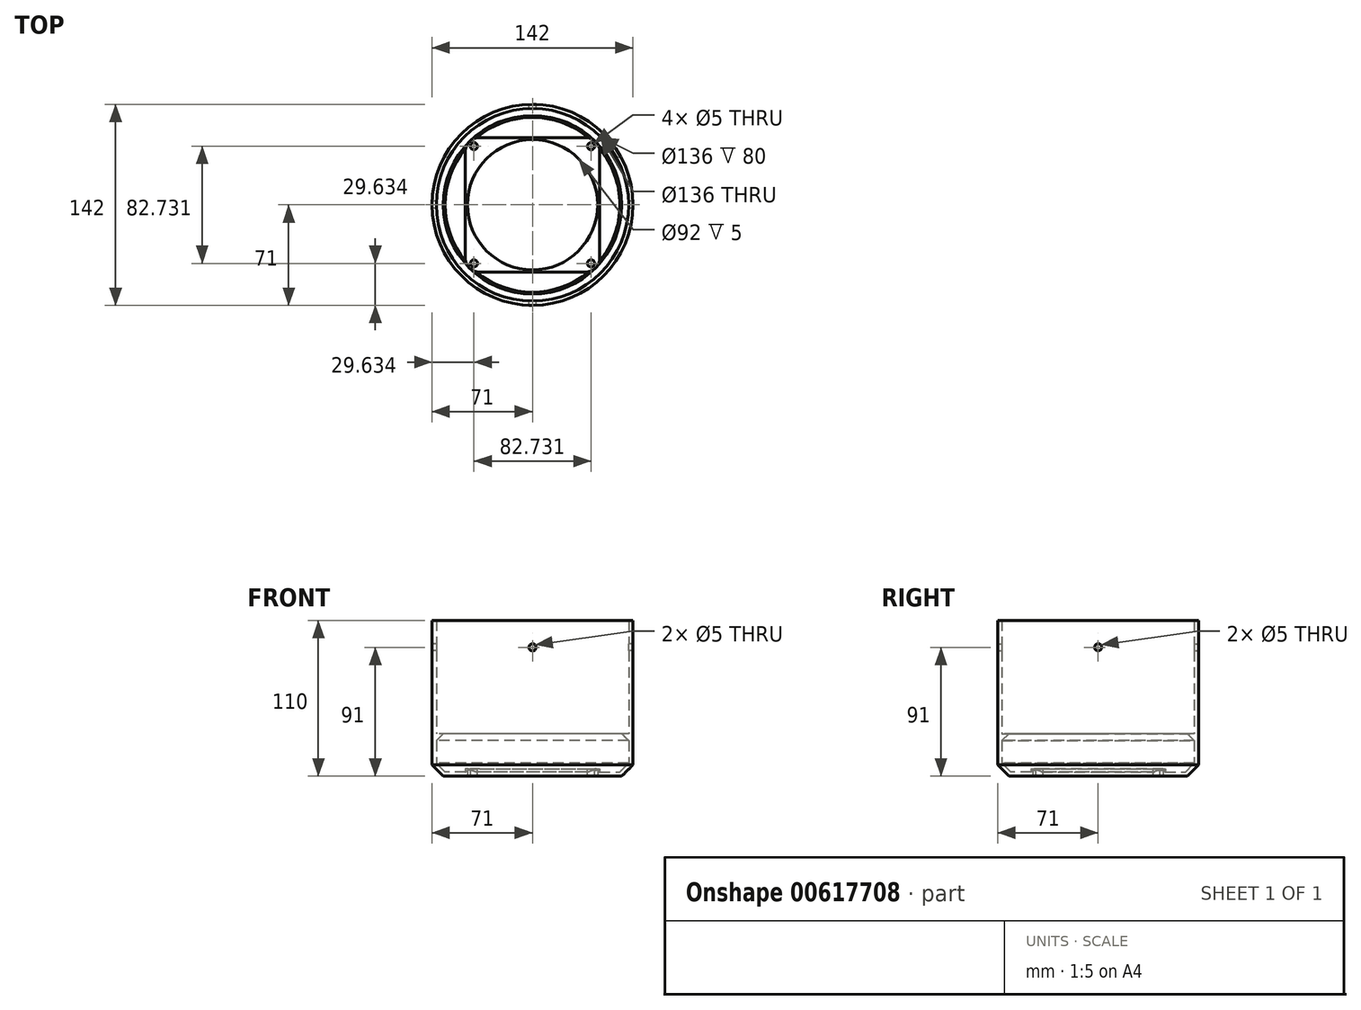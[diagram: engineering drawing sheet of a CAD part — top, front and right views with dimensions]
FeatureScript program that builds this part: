
annotation { "Feature Type Name" : "Feature", "Feature Type Description" : "" }
export const myFeature = defineFeature(function(context is Context, id is Id, definition is map)
    precondition{}
    {
        {
            var Q0;
            Q0=qCreatedBy(makeId("Top.planeOp"),FACE);
            var sketch = newSketch(context, id + "F0", { "sketchPlane" : qUnion([Q0])});
            skCircle(sketch, "E0", {"center": v(0, 0) * mm, "radius": 71 * mm});
            skSolve(sketch);
        }
        {
            var Q0;
            Q0=makeQuery(id+"F0.imprint","IMPRINT",FACE,{"disambiguationData":[TD([[makeQuery(id+"F0.imprint","IMPRINT",EDGE,{"derivedFrom":sQuery(id+"F0.wireOp",EDGE,"E0")}),1.0]])]});
            var Q1;
            Q1=sQuery(id+"F0.wireOp",EDGE,"E0");
            extrude(context, id + "F1", {"entities" : qUnion([Q0]), "surfaceEntities" : qUnion([Q1]), "depth" : 50 * mm, "offsetDistance" : 25 * mm});
        }
        {
            var Q0;
            Q0=makeQuery(id+"F1.opExtrude","CAP_EDGE",EDGE,{"disambiguationData":[OSD([sQuery(id+"F0.wireOp",EDGE,"E0")])],"isStart":true});
            chamfer(context, id + "F2", {"entities" : qUnion([Q0]), "width" : 8 * mm, "tangentPropagation" : true});
        }
        {
            var Q0;
            Q0=makeQuery(id+"F1.opExtrude","CAP_FACE",FACE,{"disambiguationData":[OSD([sQuery(id+"F0.wireOp",EDGE,"E0")])],"isStart":false});
            shell(context, id + "F3", {"entities" : qUnion([Q0]), "thickness" : 3 * mm});
        }
        {
            var Q0;
            Q0=makeQuery(id+"F1.opExtrude","CAP_FACE",FACE,{"disambiguationData":[OSD([sQuery(id+"F0.wireOp",EDGE,"E0")])],"isStart":true});
            var sketch = newSketch(context, id + "F4", { "sketchPlane" : qUnion([Q0])});
            skLineSegment(sketch, "E1.bottom", {"start": v(-37.5, 47.5) * mm, "end": v(37.5, 47.5) * mm});
            skLineSegment(sketch, "E1.top", {"start": v(-37.5, -47.5) * mm, "end": v(37.5, -47.5) * mm});
            skLineSegment(sketch, "E1.left", {"start": v(-47.5, 37.5) * mm, "end": v(-47.5, -37.5) * mm});
            skLineSegment(sketch, "E1.right", {"start": v(47.5, 37.5) * mm, "end": v(47.5, -37.5) * mm});
            skPoint(sketch, "E1.middle", {"position": v(0, 0) * mm});
            skLineSegment(sketch, "E2.bottom", {"start": v(-41.37, 41.37) * mm, "end": v(41.37, 41.37) * mm, "construction": true});
            skLineSegment(sketch, "E2.top", {"start": v(-41.37, -41.37) * mm, "end": v(41.37, -41.37) * mm, "construction": true});
            skLineSegment(sketch, "E2.left", {"start": v(-41.37, 41.37) * mm, "end": v(-41.37, -41.37) * mm, "construction": true});
            skLineSegment(sketch, "E2.right", {"start": v(41.37, 41.37) * mm, "end": v(41.37, -41.37) * mm, "construction": true});
            skCircle(sketch, "E3", {"center": v(0, 0) * mm, "radius": 46 * mm});
            skCircle(sketch, "E4", {"center": v(-41.37, 41.37) * mm, "radius": 2.5 * mm});
            skCircle(sketch, "E5", {"center": v(41.37, 41.37) * mm, "radius": 2.5 * mm});
            skCircle(sketch, "E6", {"center": v(41.37, -41.37) * mm, "radius": 2.5 * mm});
            skCircle(sketch, "E7", {"center": v(-41.37, -41.37) * mm, "radius": 2.5 * mm});
            skPoint(sketch, "E8.visualSharp", {"position": v(-47.5, 47.5) * mm});
            skArc(sketch, "E8.filletArc", {"start": v(-37.5, 47.5) * mm, "mid": v(-44.57, 44.57) * mm, "end": v(-47.5, 37.5) * mm});
            skPoint(sketch, "E9.visualSharp", {"position": v(47.5, 47.5) * mm});
            skArc(sketch, "E9.filletArc", {"start": v(47.5, 37.5) * mm, "mid": v(44.57, 44.57) * mm, "end": v(37.5, 47.5) * mm});
            skPoint(sketch, "E10.visualSharp", {"position": v(47.5, -47.5) * mm});
            skArc(sketch, "E10.filletArc", {"start": v(37.5, -47.5) * mm, "mid": v(44.57, -44.57) * mm, "end": v(47.5, -37.5) * mm});
            skPoint(sketch, "E11.visualSharp", {"position": v(-47.5, -47.5) * mm});
            skArc(sketch, "E11.filletArc", {"start": v(-47.5, -37.5) * mm, "mid": v(-44.57, -44.57) * mm, "end": v(-37.5, -47.5) * mm});
            skSolve(sketch);
        }
        {
            var Q0;
            Q0=makeQuery(id+"F4.imprint","IMPRINT",FACE,{"disambiguationData":[TD([[makeQuery(id+"F4.imprint","IMPRINT",EDGE,{"derivedFrom":sQuery(id+"F4.wireOp",EDGE,"E1.bottom")}),-1.0]])]});
            var Q1;
            Q1=makeQuery(id+"F4.imprint","IMPRINT",FACE,{"disambiguationData":[TD([[makeQuery(id+"F4.imprint","IMPRINT",EDGE,{"derivedFrom":sQuery(id+"F4.wireOp",EDGE,"E4")}),1.0]])]});
            var Q2;
            Q2=makeQuery(id+"F4.imprint","IMPRINT",FACE,{"disambiguationData":[TD([[makeQuery(id+"F4.imprint","IMPRINT",EDGE,{"derivedFrom":sQuery(id+"F4.wireOp",EDGE,"E5")}),1.0]])]});
            var Q3;
            Q3=makeQuery(id+"F4.imprint","IMPRINT",FACE,{"disambiguationData":[TD([[makeQuery(id+"F4.imprint","IMPRINT",EDGE,{"derivedFrom":sQuery(id+"F4.wireOp",EDGE,"E6")}),1.0]])]});
            var Q4;
            Q4=makeQuery(id+"F4.imprint","IMPRINT",FACE,{"disambiguationData":[TD([[makeQuery(id+"F4.imprint","IMPRINT",EDGE,{"derivedFrom":sQuery(id+"F4.wireOp",EDGE,"E7")}),1.0]])]});
            extrude(context, id + "F5", {"entities" : qUnion([Q0, Q1, Q2, Q3, Q4]), "operationType" : NewBodyOperationType.ADD, "oppositeDirection" : true, "depth" : 5 * mm, "offsetDistance" : 25 * mm});
        }
        {
            var Q0;
            Q0=makeQuery(id+"F4.imprint","IMPRINT",FACE,{"disambiguationData":[TD([[makeQuery(id+"F4.imprint","IMPRINT",EDGE,{"derivedFrom":sQuery(id+"F4.wireOp",EDGE,"E4")}),1.0]])]});
            var Q1;
            Q1=makeQuery(id+"F4.imprint","IMPRINT",FACE,{"disambiguationData":[TD([[makeQuery(id+"F4.imprint","IMPRINT",EDGE,{"derivedFrom":sQuery(id+"F4.wireOp",EDGE,"E5")}),1.0]])]});
            var Q2;
            Q2=makeQuery(id+"F4.imprint","IMPRINT",FACE,{"disambiguationData":[TD([[makeQuery(id+"F4.imprint","IMPRINT",EDGE,{"derivedFrom":sQuery(id+"F4.wireOp",EDGE,"E6")}),1.0]])]});
            var Q3;
            Q3=makeQuery(id+"F4.imprint","IMPRINT",FACE,{"disambiguationData":[TD([[makeQuery(id+"F4.imprint","IMPRINT",EDGE,{"derivedFrom":sQuery(id+"F4.wireOp",EDGE,"E7")}),1.0]])]});
            var Q4;
            Q4=makeQuery(id+"F4.imprint","IMPRINT",FACE,{"disambiguationData":[TD([[makeQuery(id+"F4.imprint","IMPRINT",EDGE,{"derivedFrom":sQuery(id+"F4.wireOp",EDGE,"E3")}),1.0]])]});
            extrude(context, id + "F6", {"entities" : qUnion([Q0, Q1, Q2, Q3, Q4]), "operationType" : NewBodyOperationType.REMOVE, "endBound" : BoundingType.SYMMETRIC, "depth" : 25 * mm, "offsetDistance" : 25 * mm});
        }
        {
            var Q0;
            Q0=qCreatedBy(makeId("Top.planeOp"),FACE);
            cPlane(context, id + "F7", {"entities" : qUnion([Q0]), "cplaneType" : CPlaneType.OFFSET, "offset" : 25 * mm, "width" : 150 * mm, "height" : 150 * mm});
        }
        {
            var Q0;
            Q0=qCreatedBy(id+"F7.planeOp",FACE);
            var sketch = newSketch(context, id + "F8", { "sketchPlane" : qUnion([Q0])});
            skPoint(sketch, "E12.middle", {"position": v(0, 0) * mm});
            skCircle(sketch, "E13", {"center": v(0, 0) * mm, "radius": 71 * mm});
            skLineSegment(sketch, "E14", {"start": v(0, 0) * mm, "end": v(0, 71) * mm});
            skLineSegment(sketch, "E15", {"start": v(0, 0) * mm, "end": v(-61.49, -35.5) * mm});
            skLineSegment(sketch, "E16", {"start": v(0, 0) * mm, "end": v(61.49, -35.5) * mm});
            skCircle(sketch, "E17", {"center": v(0, 0) * mm, "radius": 63 * mm});
            skSolve(sketch);
        }
        {
            var Q0;
            Q0 = qSketchRegion(id + "F8", true);
            extrude(context, id + "F9", {"entities" : qUnion([Q0]), "operationType" : NewBodyOperationType.ADD, "depth" : 5 * mm, "offsetDistance" : 25 * mm});
        }
        {
            var Q0;
            Q0=makeQuery(id+"F9.opExtrude","CAP_EDGE",EDGE,{"disambiguationData":[OSD([sQuery(id+"F8.wireOp",EDGE,"E17")])],"isStart":true});
            chamfer(context, id + "F10", {"entities" : qUnion([Q0]), "width" : 5 * mm, "tangentPropagation" : true});
        }
        {
            var Q0;
            Q0=makeQuery(id+"F9.opExtrude","CAP_FACE",FACE,{"disambiguationData":[OSD([sQuery(id+"F8.wireOp",EDGE,"E13"),sQuery(id+"F8.wireOp",EDGE,"E17")])],"isStart":false});
            var sketch = newSketch(context, id + "F11", { "sketchPlane" : qUnion([Q0])});
            skCircle(sketch, "E18", {"center": v(0, 0) * mm, "radius": 71 * mm});
            skCircle(sketch, "E19", {"center": v(0, 0) * mm, "radius": 68 * mm});
            skSolve(sketch);
        }
        {
            var Q0;
            Q0 = qSketchRegion(id + "F11", true);
            extrude(context, id + "F12", {"entities" : qUnion([Q0]), "operationType" : NewBodyOperationType.ADD, "depth" : 80 * mm, "offsetDistance" : 25 * mm});
        }
        {
            var Q0;
            Q0=qCreatedBy(makeId("Front.planeOp"),FACE);
            var sketch = newSketch(context, id + "F13", { "sketchPlane" : qUnion([Q0])});
            skLineSegment(sketch, "E20", {"start": v(0, -12.77) * mm, "end": v(0, 86.39) * mm, "construction": true});
            skLineSegment(sketch, "E21", {"start": v(-7.06, 91) * mm, "end": v(8.94, 91) * mm, "construction": true});
            skCircle(sketch, "E22", {"center": v(0, 91) * mm, "radius": 2.5 * mm});
            skSolve(sketch);
        }
        {
            var Q0;
            Q0 = qSketchRegion(id + "F13", true);
            extrude(context, id + "F14", {"entities" : qUnion([Q0]), "operationType" : NewBodyOperationType.REMOVE, "endBound" : BoundingType.SYMMETRIC, "depth" : 150 * mm, "offsetDistance" : 25 * mm});
        }
        {
            var Q0;
            Q0=qCreatedBy(makeId("Right.planeOp"),FACE);
            var sketch = newSketch(context, id + "F15", { "sketchPlane" : qUnion([Q0])});
            skLineSegment(sketch, "E23", {"start": v(0, 182.8) * mm, "end": v(0, -29.5) * mm, "construction": true});
            skLineSegment(sketch, "E24", {"start": v(-16.38, 91) * mm, "end": v(15.93, 91) * mm, "construction": true});
            skCircle(sketch, "E25", {"center": v(0, 91) * mm, "radius": 2.5 * mm});
            skSolve(sketch);
        }
        {
            var Q0;
            Q0 = qSketchRegion(id + "F15", true);
            extrude(context, id + "F16", {"entities" : qUnion([Q0]), "operationType" : NewBodyOperationType.REMOVE, "endBound" : BoundingType.SYMMETRIC, "depth" : 150 * mm, "offsetDistance" : 25 * mm});
        }
    });
